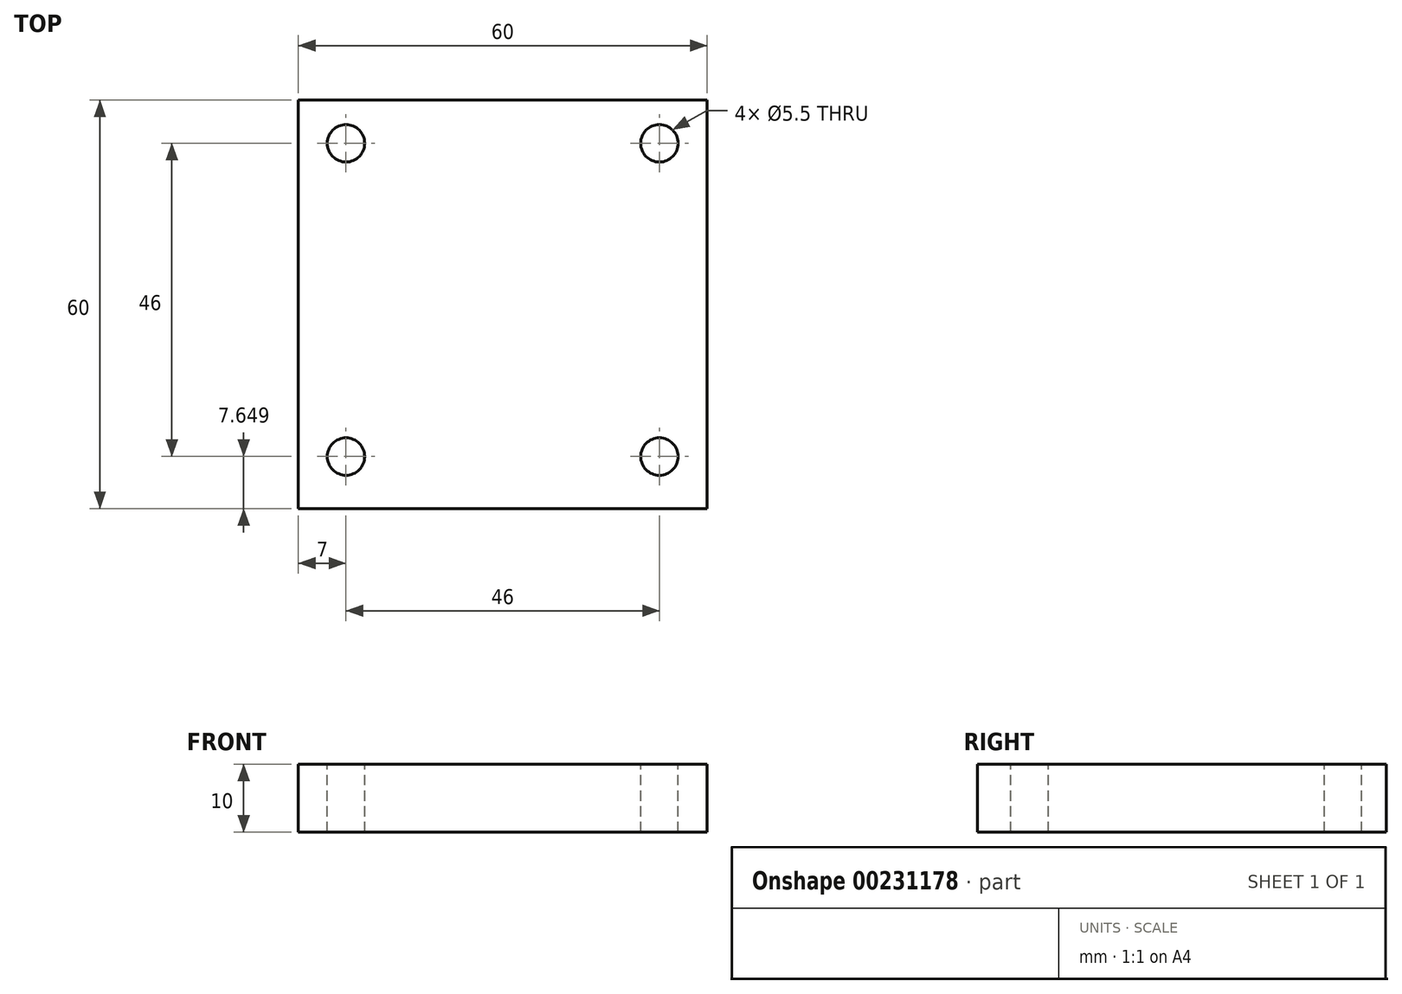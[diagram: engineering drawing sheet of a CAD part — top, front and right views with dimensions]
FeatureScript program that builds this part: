
annotation { "Feature Type Name" : "Feature", "Feature Type Description" : "" }
export const myFeature = defineFeature(function(context is Context, id is Id, definition is map)
    precondition{}
    {
        {
            var Q0;
            Q0=qCreatedBy(makeId("Top.planeOp"),FACE);
            var sketch = newSketch(context, id + "F0", { "sketchPlane" : qUnion([Q0])});
            skLineSegment(sketch, "E0.bottom", {"start": v(30, 30) * mm, "end": v(-30, 30) * mm});
            skLineSegment(sketch, "E0.top", {"start": v(30, -30) * mm, "end": v(-30, -30) * mm});
            skLineSegment(sketch, "E0.left", {"start": v(30, 30) * mm, "end": v(30, -30) * mm});
            skLineSegment(sketch, "E0.right", {"start": v(-30, 30) * mm, "end": v(-30, -30) * mm});
            skPoint(sketch, "E0.middle", {"position": v(0, 0) * mm});
            skSolve(sketch);
        }
        {
            var Q0;
            Q0=makeQuery(id+"F0.imprint","IMPRINT",FACE,{"disambiguationData":[TD([[makeQuery(id+"F0.imprint","IMPRINT",EDGE,{"derivedFrom":sQuery(id+"F0.wireOp",EDGE,"E0.bottom")}),1.0]])]});
            extrude(context, id + "F1", {"entities" : qUnion([Q0]), "oppositeDirection" : true, "depth" : 10 * mm});
        }
        {
            var Q0;
            Q0=makeQuery(id+"F1.opExtrude","CAP_FACE",FACE,{"disambiguationData":[OSD([sQuery(id+"F0.wireOp",EDGE,"E0.bottom"),sQuery(id+"F0.wireOp",EDGE,"E0.top"),sQuery(id+"F0.wireOp",EDGE,"E0.left"),sQuery(id+"F0.wireOp",EDGE,"E0.right")])],"isStart":true});
            var sketch = newSketch(context, id + "F2", { "sketchPlane" : qUnion([Q0])});
            skLineSegment(sketch, "E1.bottom", {"start": v(-23, 23.65) * mm, "end": v(23, 23.65) * mm, "construction": true});
            skLineSegment(sketch, "E1.top", {"start": v(-23, -22.35) * mm, "end": v(23, -22.35) * mm, "construction": true});
            skLineSegment(sketch, "E1.left", {"start": v(-23, 23.65) * mm, "end": v(-23, -22.35) * mm, "construction": true});
            skLineSegment(sketch, "E1.right", {"start": v(23, 23.65) * mm, "end": v(23, -22.35) * mm, "construction": true});
            skPoint(sketch, "E1.middle", {"position": v(0, 0.65) * mm});
            skSolve(sketch);
        }
        {
            var Q0;
            Q0=sQuery(id+"F2.wireOp",VERTEX,"E1.top.end");
            var Q1;
            Q1=sQuery(id+"F2.wireOp",VERTEX,"E1.left.end");
            var Q2;
            Q2=sQuery(id+"F2.wireOp",VERTEX,"E1.left.start");
            var Q3;
            Q3=sQuery(id+"F2.wireOp",VERTEX,"E1.right.start");
            var Q4;
            Q4=makeQuery(id+"F1.opExtrude","SWEPT_BODY",BODY,{"disambiguationData":[OSD([sQuery(id+"F0.wireOp",EDGE,"E0.bottom"),sQuery(id+"F0.wireOp",EDGE,"E0.top"),sQuery(id+"F0.wireOp",EDGE,"E0.left"),sQuery(id+"F0.wireOp",EDGE,"E0.right")])]});
            hole(context, id + "F3", {"style" : HoleStyle.SIMPLE, "endStyle" : HoleEndStyle.THROUGH, "standardTappedOrClearance" : lookupTablePath({ "standard" : "ISO", "fit" : "Normal", "size" : "M5", "type" : "Clearance" }), "standardBlindInLast" : lookupTablePath({ "fit" : "Standard", "standard" : "ISO", "size" : "M5", "type" : "Clearance" }), "holeDiameter" : 5.5 * mm, "locations" : qUnion([Q0, Q1, Q2, Q3]), "scope" : qUnion([Q4]), "isTappedThrough" : true});
        }
    });
